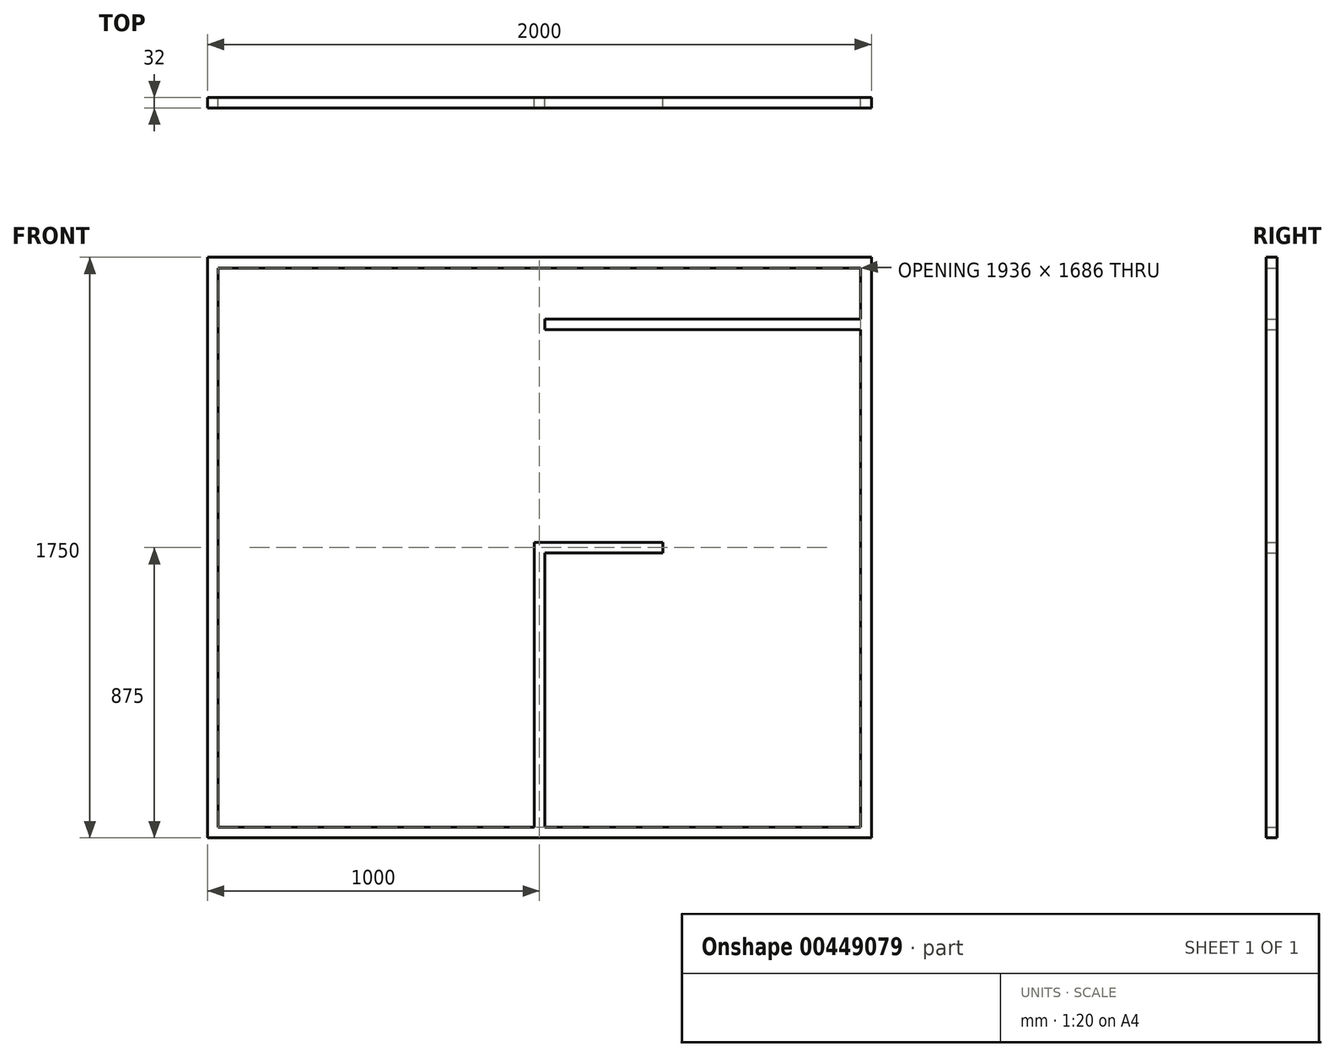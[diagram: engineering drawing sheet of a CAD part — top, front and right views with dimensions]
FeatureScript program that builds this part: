
annotation { "Feature Type Name" : "Feature", "Feature Type Description" : "" }
export const myFeature = defineFeature(function(context is Context, id is Id, definition is map)
    precondition{}
    {
        {
            var Q0;
            Q0=qCreatedBy(makeId("Front.planeOp"),FACE);
            var sketch = newSketch(context, id + "F0", { "sketchPlane" : qUnion([Q0])});
            skLineSegment(sketch, "E0.bottom", {"start": v(0, 0) * mm, "end": v(2000, 0) * mm});
            skLineSegment(sketch, "E0.top", {"start": v(0, 1750) * mm, "end": v(2000, 1750) * mm});
            skLineSegment(sketch, "E0.left", {"start": v(0, 0) * mm, "end": v(0, 1750) * mm});
            skLineSegment(sketch, "E0.right", {"start": v(2000, 0) * mm, "end": v(2000, 1750) * mm});
            skLineSegment(sketch, "E1.0", {"start": v(32, 32) * mm, "end": v(32, 1718) * mm});
            skLineSegment(sketch, "E1.1", {"start": v(32, 32) * mm, "end": v(1968, 32) * mm});
            skLineSegment(sketch, "E1.2", {"start": v(1968, 32) * mm, "end": v(1968, 1718) * mm});
            skLineSegment(sketch, "E1.3", {"start": v(32, 1718) * mm, "end": v(1968, 1718) * mm});
            skLineSegment(sketch, "E2", {"start": v(1000, 1718) * mm, "end": v(1000, 32) * mm, "construction": true});
            skLineSegment(sketch, "E3", {"start": v(32, 875) * mm, "end": v(1968, 875) * mm, "construction": true});
            skLineSegment(sketch, "E4.bottom", {"start": v(984, 1718) * mm, "end": v(1016, 1718) * mm});
            skLineSegment(sketch, "E4.top", {"start": v(984, 32) * mm, "end": v(1016, 32) * mm});
            skLineSegment(sketch, "E4.left", {"start": v(984, 1718) * mm, "end": v(984, 32) * mm});
            skLineSegment(sketch, "E4.right", {"start": v(1016, 1718) * mm, "end": v(1016, 32) * mm});
            skLineSegment(sketch, "E5.left", {"start": v(1968, 891) * mm, "end": v(1968, 859) * mm});
            skLineSegment(sketch, "E5.right", {"start": v(32, 891) * mm, "end": v(32, 859) * mm});
            skLineSegment(sketch, "E6", {"start": v(1968, 875) * mm, "end": v(1926.84, 875) * mm, "construction": true});
            skLineSegment(sketch, "E7", {"start": v(1000, 1718) * mm, "end": v(1000, 1691.84) * mm, "construction": true});
            skLineSegment(sketch, "E8.bottom", {"start": v(1404, 32) * mm, "end": v(1372, 32) * mm});
            skLineSegment(sketch, "E8.top", {"start": v(1404, 1532) * mm, "end": v(1372, 1532) * mm});
            skLineSegment(sketch, "E8.left", {"start": v(1404, 32) * mm, "end": v(1404, 1532) * mm});
            skLineSegment(sketch, "E8.right", {"start": v(1372, 32) * mm, "end": v(1372, 1532) * mm});
            skLineSegment(sketch, "E9.bottom", {"start": v(1016, 1532) * mm, "end": v(1968, 1532) * mm});
            skLineSegment(sketch, "E9.top", {"start": v(1016, 1564) * mm, "end": v(1968, 1564) * mm});
            skLineSegment(sketch, "E9.left", {"start": v(1016, 1532) * mm, "end": v(1016, 1564) * mm});
            skLineSegment(sketch, "E9.right", {"start": v(1968, 1532) * mm, "end": v(1968, 1564) * mm});
            skLineSegment(sketch, "E10.trimOffspring", {"start": v(1372, 859) * mm, "end": v(32, 859) * mm});
            skLineSegment(sketch, "E11.trimOffspring", {"start": v(1372, 891) * mm, "end": v(32, 891) * mm});
            skSolve(sketch);
        }
        {
            var Q0;
            Q0 = qSketchRegion(id + "F0", true);
            var Q1;
            {var subQ5=sQuery(id+"F0.wireOp",EDGE,"E5.right");Q1=makeQuery(id+"F0.imprint","IMPRINT",FACE,{"disambiguationData":[TD([[makeQuery(id+"F0.imprint","IMPRINT",EDGE,{"derivedFrom":subQ5}),1.0]])]});}
            var Q2;
            {var subQ0=sQuery(id+"F0.wireOp",EDGE,"E4.bottom");Q2=makeQuery(id+"F0.imprint","IMPRINT",FACE,{"disambiguationData":[TD([[makeQuery(id+"F0.imprint","IMPRINT",EDGE,{"derivedFrom":subQ0}),-1.0]])]});}
            var Q3;
            {var subQ0=sQuery(id+"F0.wireOp",EDGE,"E5.bottom");var subQ1=sQuery(id+"F0.wireOp",EDGE,"E4.left");var subQ2=makeQuery(id+"F0.imprint","INTERSECT",VERTEX,{"derivedFrom":[subQ1,subQ0]});Q3=makeQuery(id+"F0.imprint","IMPRINT",FACE,{"disambiguationData":[TD([[makeQuery(id+"F0.imprint","IMPRINT",EDGE,{"disambiguationData":[TD([[subQ2,-1.0]])],"derivedFrom":subQ1}),1.0]])]});}
            var Q4;
            {var subQ0=sQuery(id+"F0.wireOp",EDGE,"E4.top");Q4=makeQuery(id+"F0.imprint","IMPRINT",FACE,{"disambiguationData":[TD([[makeQuery(id+"F0.imprint","IMPRINT",EDGE,{"derivedFrom":subQ0}),1.0]])]});}
            var Q5;
            {var subQ0=sQuery(id+"F0.wireOp",EDGE,"E11.trimOffspring");var subQ1=sQuery(id+"F0.wireOp",EDGE,"E4.right");var subQ2=makeQuery(id+"F0.imprint","INTERSECT",VERTEX,{"derivedFrom":[subQ1,subQ0]});Q5=makeQuery(id+"F0.imprint","IMPRINT",FACE,{"disambiguationData":[TD([[makeQuery(id+"F0.imprint","IMPRINT",EDGE,{"disambiguationData":[TD([[subQ2,-1.0]])],"derivedFrom":subQ1}),1.0]])]});}
            var Q6;
            {var subQ3=sQuery(id+"F0.wireOp",EDGE,"E8.bottom");Q6=makeQuery(id+"F0.imprint","IMPRINT",FACE,{"disambiguationData":[TD([[makeQuery(id+"F0.imprint","IMPRINT",EDGE,{"derivedFrom":subQ3}),-1.0]])]});}
            var Q7;
            Q7=makeQuery(id+"F0.imprint","IMPRINT",FACE,{"disambiguationData":[TD([[makeQuery(id+"F0.imprint","IMPRINT",EDGE,{"derivedFrom":sQuery(id+"F0.wireOp",EDGE,"E9.top")}),-1.0]])]});
            extrude(context, id + "F1", {"entities" : qUnion([Q0, Q1, Q2, Q3, Q4, Q5, Q6, Q7]), "depth" : 32 * mm});
        }
    });
